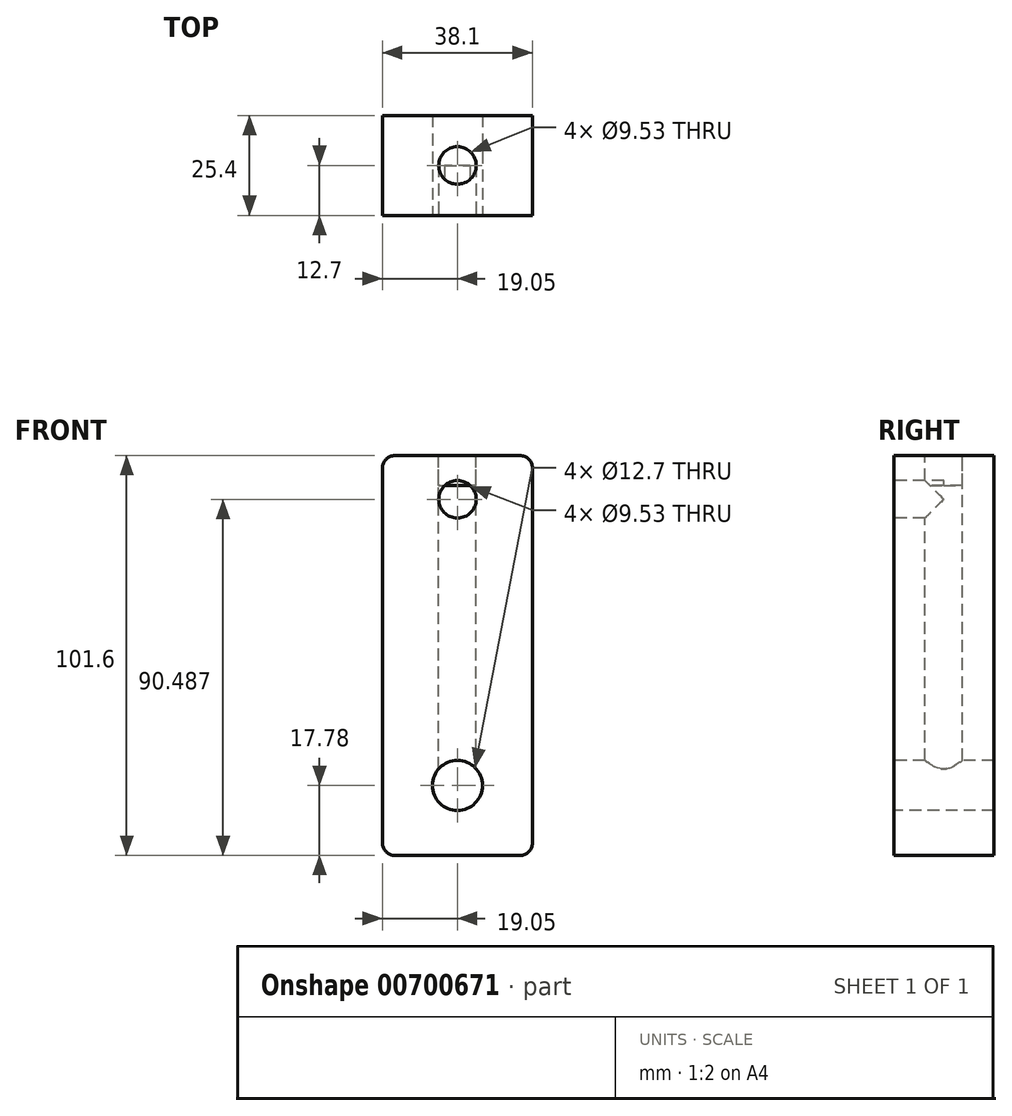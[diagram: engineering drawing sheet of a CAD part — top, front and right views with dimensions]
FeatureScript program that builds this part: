
annotation { "Feature Type Name" : "Feature", "Feature Type Description" : "" }
export const myFeature = defineFeature(function(context is Context, id is Id, definition is map)
    precondition{}
    {
        {
            var Q0;
            Q0=qCreatedBy(makeId("Front.planeOp"),FACE);
            var sketch = newSketch(context, id + "F0", { "sketchPlane" : qUnion([Q0])});
            skLineSegment(sketch, "E0.bottom", {"start": v(3.18, 0) * mm, "end": v(34.93, 0) * mm});
            skLineSegment(sketch, "E0.top", {"start": v(3.17, 101.6) * mm, "end": v(34.92, 101.6) * mm});
            skLineSegment(sketch, "E0.left", {"start": v(0, 3.17) * mm, "end": v(0, 98.43) * mm});
            skLineSegment(sketch, "E0.right", {"start": v(38.1, 3.17) * mm, "end": v(38.1, 98.43) * mm});
            skPoint(sketch, "E1.visualSharp", {"position": v(0, 101.6) * mm});
            skArc(sketch, "E1.filletArc", {"start": v(3.17, 101.6) * mm, "mid": v(0.93, 100.67) * mm, "end": v(0, 98.43) * mm});
            skPoint(sketch, "E2.visualSharp", {"position": v(38.1, 101.6) * mm});
            skArc(sketch, "E2.filletArc", {"start": v(38.1, 98.43) * mm, "mid": v(37.17, 100.67) * mm, "end": v(34.92, 101.6) * mm});
            skPoint(sketch, "E3.visualSharp", {"position": v(38.1, 0) * mm});
            skArc(sketch, "E3.filletArc", {"start": v(34.93, 0) * mm, "mid": v(37.17, 0.93) * mm, "end": v(38.1, 3.18) * mm});
            skPoint(sketch, "E4.visualSharp", {"position": v(0, 0) * mm});
            skArc(sketch, "E4.filletArc", {"start": v(0, 3.17) * mm, "mid": v(0.93, 0.93) * mm, "end": v(3.18, 0) * mm});
            skSolve(sketch);
        }
        {
            var Q0;
            Q0 = qSketchRegion(id + "F0", true);
            extrude(context, id + "F1", {"entities" : qUnion([Q0]), "depth" : 25.4 * mm, "offsetDistance" : 25.4 * mm});
        }
        {
            var Q0;
            Q0=makeQuery(id+"F1.opExtrude","CAP_FACE",FACE,{"disambiguationData":[OSD([sQuery(id+"F0.wireOp",EDGE,"E0.bottom"),sQuery(id+"F0.wireOp",EDGE,"E0.top"),sQuery(id+"F0.wireOp",EDGE,"E0.left"),sQuery(id+"F0.wireOp",EDGE,"E0.right"),sQuery(id+"F0.wireOp",EDGE,"E1.filletArc"),sQuery(id+"F0.wireOp",EDGE,"E2.filletArc"),sQuery(id+"F0.wireOp",EDGE,"E3.filletArc"),sQuery(id+"F0.wireOp",EDGE,"E4.filletArc")])],"isStart":false});
            var sketch = newSketch(context, id + "F2", { "sketchPlane" : qUnion([Q0])});
            skCircle(sketch, "E5", {"center": v(19.05, 17.78) * mm, "radius": 6.35 * mm});
            skPoint(sketch, "E6", {"position": v(12.7, 17.78) * mm});
            skPoint(sketch, "E7", {"position": v(25.4, 17.78) * mm});
            skPoint(sketch, "E8", {"position": v(19.05, 11.43) * mm});
            skPoint(sketch, "E8.positionSnap0", {"position": v(19.05, 0) * mm});
            skPoint(sketch, "E9", {"position": v(38.1, 17.78) * mm});
            skPoint(sketch, "E10", {"position": v(0, 17.78) * mm});
            skSolve(sketch);
        }
        {
            var Q0;
            Q0 = qSketchRegion(id + "F2", true);
            extrude(context, id + "F3", {"entities" : qUnion([Q0]), "operationType" : NewBodyOperationType.REMOVE, "oppositeDirection" : true, "depth" : 127 * mm, "offsetDistance" : 25.4 * mm});
        }
        {
            var Q0;
            Q0=makeQuery(id+"F1.opExtrude","SWEPT_FACE",FACE,{"disambiguationData":[OSD([sQuery(id+"F0.wireOp",EDGE,"E0.top")])]});
            var sketch = newSketch(context, id + "F4", { "sketchPlane" : qUnion([Q0])});
            skPoint(sketch, "E11", {"position": v(19.05, -12.7) * mm});
            skPoint(sketch, "E11.positionSnap0", {"position": v(3.17, -12.7) * mm});
            skPoint(sketch, "E11.positionSnap1", {"position": v(19.05, 0) * mm});
            skCircle(sketch, "E12", {"center": v(19.05, -12.7) * mm, "radius": 4.76 * mm});
            skSolve(sketch);
        }
        {
            var Q0;
            Q0 = qSketchRegion(id + "F4", true);
            extrude(context, id + "F5", {"entities" : qUnion([Q0]), "operationType" : NewBodyOperationType.REMOVE, "oppositeDirection" : true, "depth" : 81.28 * mm, "offsetDistance" : 25.4 * mm});
        }
        {
            var Q0;
            Q0=makeQuery(id+"F1.opExtrude","CAP_FACE",FACE,{"disambiguationData":[OSD([sQuery(id+"F0.wireOp",EDGE,"E0.bottom"),sQuery(id+"F0.wireOp",EDGE,"E0.top"),sQuery(id+"F0.wireOp",EDGE,"E0.left"),sQuery(id+"F0.wireOp",EDGE,"E0.right"),sQuery(id+"F0.wireOp",EDGE,"E1.filletArc"),sQuery(id+"F0.wireOp",EDGE,"E2.filletArc"),sQuery(id+"F0.wireOp",EDGE,"E3.filletArc"),sQuery(id+"F0.wireOp",EDGE,"E4.filletArc")])],"isStart":false});
            var sketch = newSketch(context, id + "F6", { "sketchPlane" : qUnion([Q0])});
            skCircle(sketch, "E13", {"center": v(19.05, 90.49) * mm, "radius": 4.76 * mm});
            skPoint(sketch, "E13.centerSnap0", {"position": v(19.05, 101.6) * mm});
            skSolve(sketch);
        }
        {
            var Q0;
            Q0=makeQuery(id+"F1.opExtrude","SWEPT_FACE",FACE,{"disambiguationData":[OSD([sQuery(id+"F0.wireOp",EDGE,"E0.top")])]});
            var sketch = newSketch(context, id + "F7", { "sketchPlane" : qUnion([Q0])});
            skCircle(sketch, "E14.0", {"center": v(19.05, -12.7) * mm, "radius": 4.76 * mm});
            skSolve(sketch);
        }
        {
            var Q0;
            Q0 = qSketchRegion(id + "F7", true);
            extrude(context, id + "F8", {"entities" : qUnion([Q0]), "oppositeDirection" : true, "depth" : 7.62 * mm, "offsetDistance" : 25.4 * mm});
        }
        {
            var Q0;
            Q0 = qSketchRegion(id + "F6", true);
            extrude(context, id + "F9", {"entities" : qUnion([Q0]), "operationType" : NewBodyOperationType.REMOVE, "oppositeDirection" : true, "depth" : 12.7 * mm, "offsetDistance" : 25.4 * mm});
        }
    });
